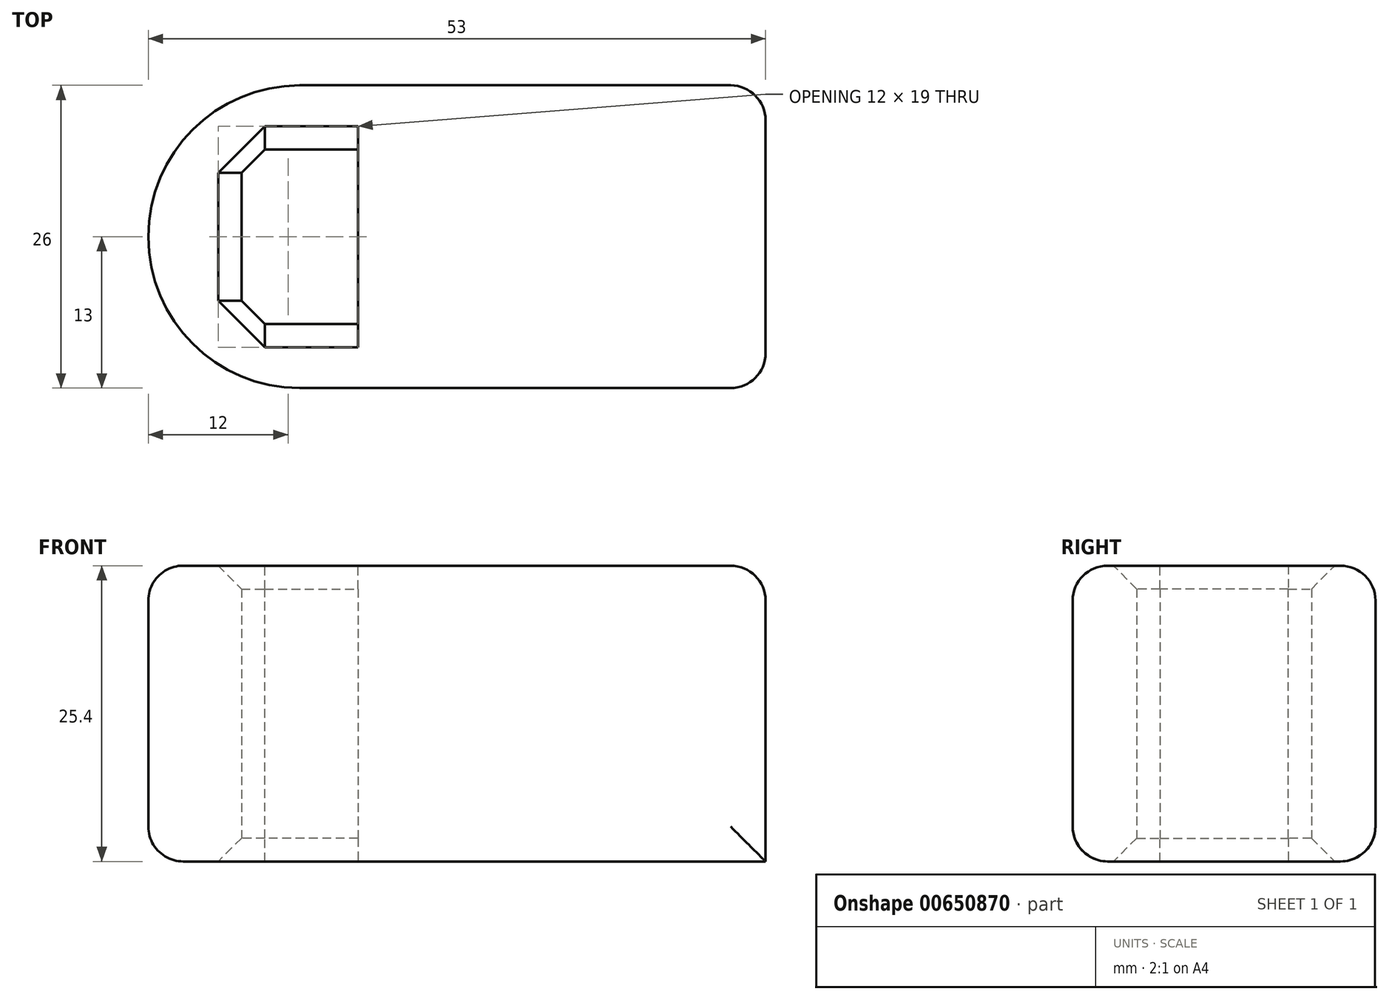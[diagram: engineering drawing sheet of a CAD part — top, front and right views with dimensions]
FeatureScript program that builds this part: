
annotation { "Feature Type Name" : "Feature", "Feature Type Description" : "" }
export const myFeature = defineFeature(function(context is Context, id is Id, definition is map)
    precondition{}
    {
        {
            var Q0;
            Q0=qCreatedBy(makeId("Top.planeOp"),FACE);
            var sketch = newSketch(context, id + "F0", { "sketchPlane" : qUnion([Q0])});
            skArc(sketch, "E0", {"start": v(0, 13) * mm, "mid": v(-13, 0) * mm, "end": v(0, -13) * mm});
            skLineSegment(sketch, "E1", {"start": v(0, 13) * mm, "end": v(40, 13) * mm});
            skLineSegment(sketch, "E2", {"start": v(0, -13) * mm, "end": v(40, -13) * mm});
            skLineSegment(sketch, "E3", {"start": v(40, -13) * mm, "end": v(40, 13) * mm});
            skLineSegment(sketch, "E4.bottom", {"start": v(5, -7.5) * mm, "end": v(-5, -7.5) * mm});
            skLineSegment(sketch, "E4.top", {"start": v(5, 7.5) * mm, "end": v(-5, 7.5) * mm});
            skLineSegment(sketch, "E4.left", {"start": v(5, -7.5) * mm, "end": v(5, 7.5) * mm});
            skLineSegment(sketch, "E4.right", {"start": v(-5, -7.5) * mm, "end": v(-5, 7.5) * mm});
            skPoint(sketch, "E5.middle", {"position": v(5, 0) * mm});
            skLineSegment(sketch, "E6.left", {"start": v(-5, 0) * mm, "end": v(-5, 0) * mm});
            skSolve(sketch);
        }
        {
            var Q0;
            Q0=makeQuery(id+"F0.imprint","IMPRINT",FACE,{"disambiguationData":[TD([[makeQuery(id+"F0.imprint","IMPRINT",EDGE,{"derivedFrom":sQuery(id+"F0.wireOp",EDGE,"E0")}),1.0]])]});
            extrude(context, id + "F1", {"entities" : qUnion([Q0]), "depth" : 25.4 * mm, "offsetDistance" : 25.4 * mm});
        }
        {
            var Q0;
            Q0=makeQuery(id+"F1.opExtrude","CAP_EDGE",EDGE,{"disambiguationData":[OSD([sQuery(id+"F0.wireOp",EDGE,"E2")])],"isStart":false});
            var Q1;
            Q1=makeQuery(id+"F1.opExtrude","CAP_EDGE",EDGE,{"disambiguationData":[OSD([sQuery(id+"F0.wireOp",EDGE,"E3")])],"isStart":false});
            var Q2;
            Q2=makeQuery(id+"F1.opExtrude","SWEPT_EDGE",EDGE,{"disambiguationData":[OSD([sQuery(id+"F0.wireOp",EDGE,"E2"),sQuery(id+"F0.wireOp",EDGE,"E3")])]});
            var Q3;
            Q3=makeQuery(id+"F1.opExtrude","SWEPT_EDGE",EDGE,{"disambiguationData":[OSD([sQuery(id+"F0.wireOp",EDGE,"E1"),sQuery(id+"F0.wireOp",EDGE,"E3")])]});
            var Q4;
            Q4=makeQuery(id+"F1.opExtrude","CAP_EDGE",EDGE,{"disambiguationData":[OSD([sQuery(id+"F0.wireOp",EDGE,"E2")])],"isStart":true});
            fillet(context, id + "F2", {"entities" : qUnion([Q0, Q1, Q2, Q3, Q4]), "radius" : 3 * mm, "tangentPropagation" : true, "allowEdgeOverflow" : false});
        }
        {
            var Q0;
            Q0=makeQuery(id+"F1.opExtrude","SWEPT_FACE",FACE,{"disambiguationData":[OSD([sQuery(id+"F0.wireOp",EDGE,"E4.right")])]});
            chamfer(context, id + "F3", {"entities" : qUnion([Q0]), "width" : 2 * mm, "tangentPropagation" : true});
        }
    });
